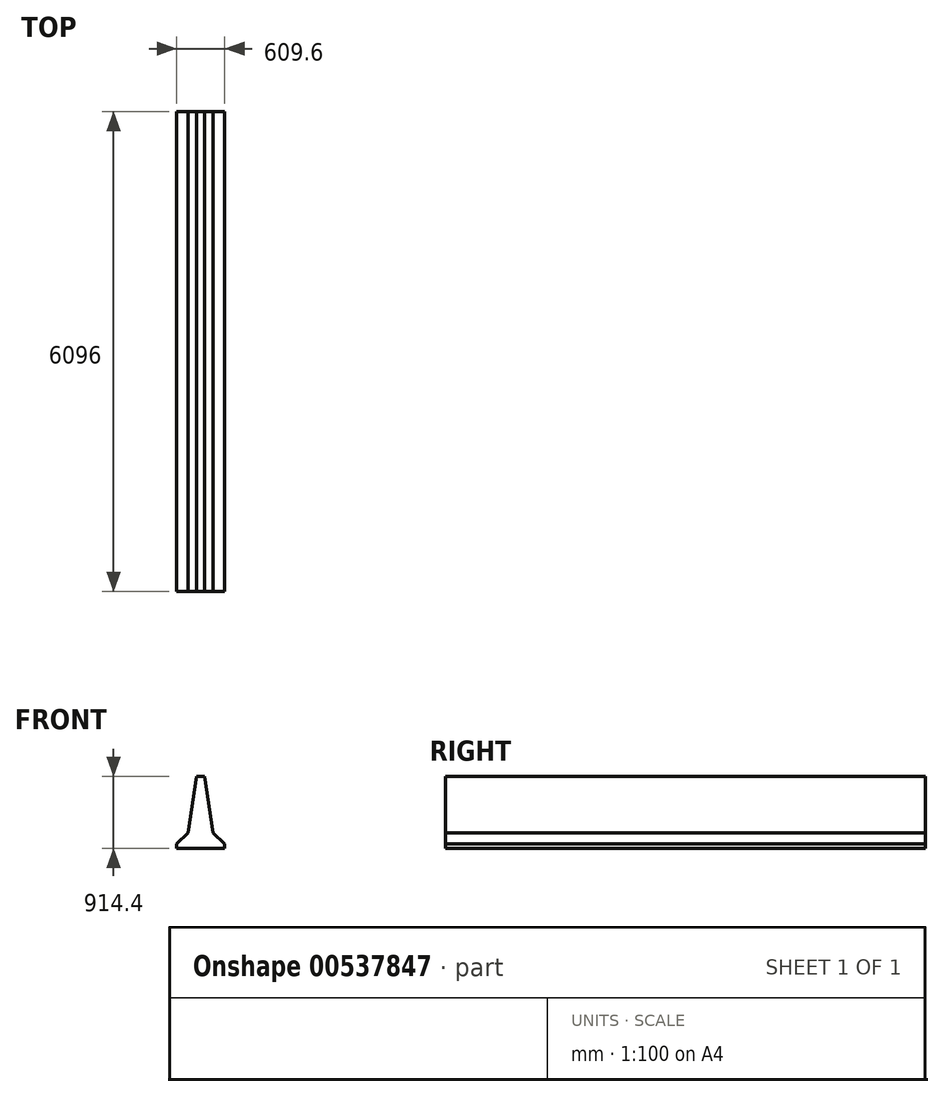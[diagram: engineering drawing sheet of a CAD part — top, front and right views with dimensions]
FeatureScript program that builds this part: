
annotation { "Feature Type Name" : "Feature", "Feature Type Description" : "" }
export const myFeature = defineFeature(function(context is Context, id is Id, definition is map)
    precondition{}
    {
        {
            var Q0;
            Q0=qCreatedBy(makeId("Front.planeOp"),FACE);
            var sketch = newSketch(context, id + "F0", { "sketchPlane" : qUnion([Q0])});
            skLineSegment(sketch, "E0", {"start": v(0, 0) * mm, "end": v(304.8, 0) * mm});
            skLineSegment(sketch, "E1", {"start": v(304.8, 0) * mm, "end": v(304.8, 60.2) * mm});
            skLineSegment(sketch, "E2", {"start": v(304.8, 60.2) * mm, "end": v(158.38, 195.94) * mm});
            skLineSegment(sketch, "E3", {"start": v(158.38, 195.94) * mm, "end": v(50.8, 914.4) * mm});
            skLineSegment(sketch, "E4", {"start": v(50.8, 914.4) * mm, "end": v(0, 914.4) * mm});
            skLineSegment(sketch, "E5.MirrorCS", {"start": v(0, 0) * mm, "end": v(-304.8, 0) * mm});
            skLineSegment(sketch, "E6.MirrorCS", {"start": v(-304.8, 60.2) * mm, "end": v(-158.38, 195.94) * mm});
            skLineSegment(sketch, "E7.MirrorCS", {"start": v(-304.8, 0) * mm, "end": v(-304.8, 60.2) * mm});
            skLineSegment(sketch, "E8.MirrorCS", {"start": v(-158.38, 195.94) * mm, "end": v(-50.8, 914.4) * mm});
            skLineSegment(sketch, "E9.MirrorCS", {"start": v(-50.8, 914.4) * mm, "end": v(0, 914.4) * mm});
            skSolve(sketch);
        }
        {
            var Q0;
            Q0=makeQuery(id+"F0.imprint","IMPRINT",FACE,{"disambiguationData":[TD([[makeQuery(id+"F0.imprint","IMPRINT",EDGE,{"derivedFrom":sQuery(id+"F0.wireOp",EDGE,"E0")}),1.0]])]});
            extrude(context, id + "F1", {"entities" : qUnion([Q0]), "depth" : 6096 * mm, "offsetDistance" : 25.4 * mm});
        }
    });
